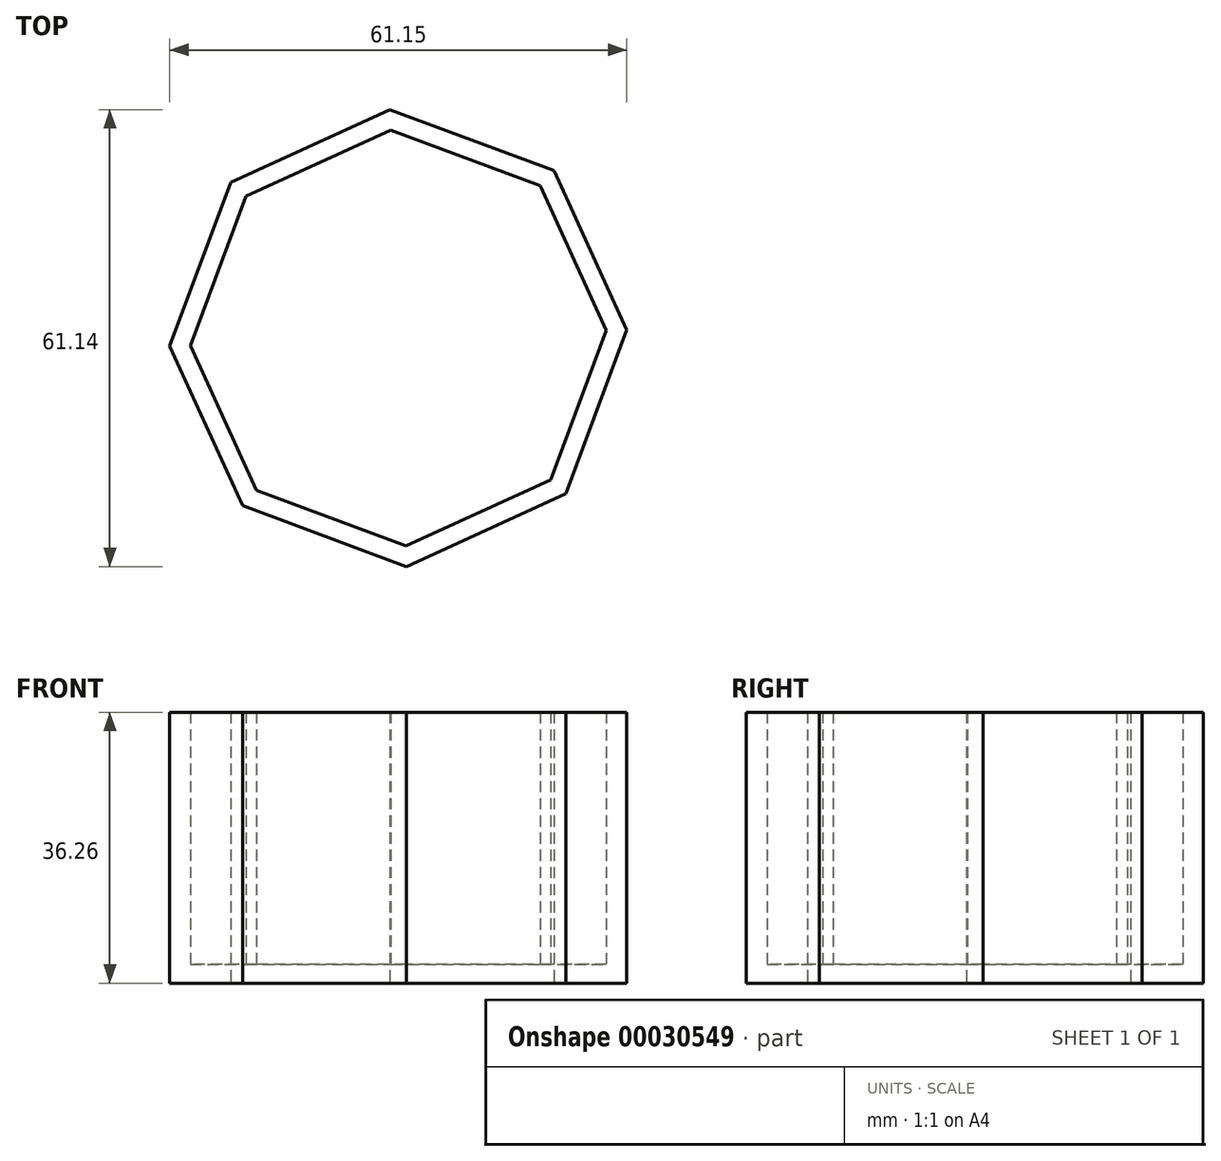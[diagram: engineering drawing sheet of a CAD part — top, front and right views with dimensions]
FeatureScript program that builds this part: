
annotation { "Feature Type Name" : "Feature", "Feature Type Description" : "" }
export const myFeature = defineFeature(function(context is Context, id is Id, definition is map)
    precondition{}
    {
        {
            var Q0;
            Q0=qCreatedBy(makeId("Top.planeOp"),FACE);
            var sketch = newSketch(context, id + "F0", { "sketchPlane" : qUnion([Q0])});
            skCircle(sketch, "E0.cCircle", {"center": v(-38.84, -19.02) * mm, "radius": 28.26 * mm, "construction": true});
            skLineSegment(sketch, "E0.0", {"start": v(-18, 3.38) * mm, "end": v(-8.26, -17.92) * mm});
            skLineSegment(sketch, "E0.1", {"start": v(-8.26, -17.92) * mm, "end": v(-16.44, -39.86) * mm});
            skLineSegment(sketch, "E0.2", {"start": v(-16.44, -39.86) * mm, "end": v(-37.74, -49.6) * mm});
            skLineSegment(sketch, "E0.3", {"start": v(-37.74, -49.6) * mm, "end": v(-59.68, -41.42) * mm});
            skLineSegment(sketch, "E0.4", {"start": v(-59.68, -41.42) * mm, "end": v(-69.41, -20.12) * mm});
            skLineSegment(sketch, "E0.5", {"start": v(-69.41, -20.12) * mm, "end": v(-61.23, 1.82) * mm});
            skLineSegment(sketch, "E0.6", {"start": v(-61.23, 1.82) * mm, "end": v(-39.94, 11.55) * mm});
            skLineSegment(sketch, "E0.7", {"start": v(-39.94, 11.55) * mm, "end": v(-18, 3.38) * mm});
            skPoint(sketch, "E0.0.midPoint", {"position": v(-13.13, -7.27) * mm});
            skSolve(sketch);
        }
        {
            var Q0;
            Q0 = qSketchRegion(id + "F0", true);
            extrude(context, id + "F1", {"entities" : qUnion([Q0]), "depth" : 10.86 * mm});
        }
        {
            var Q0;
            Q0=makeQuery(id+"F1.opExtrude","CAP_FACE",FACE,{"disambiguationData":[OSD([sQuery(id+"F0.wireOp",EDGE,"E0.0"),sQuery(id+"F0.wireOp",EDGE,"E0.1"),sQuery(id+"F0.wireOp",EDGE,"E0.2"),sQuery(id+"F0.wireOp",EDGE,"E0.3"),sQuery(id+"F0.wireOp",EDGE,"E0.4"),sQuery(id+"F0.wireOp",EDGE,"E0.5"),sQuery(id+"F0.wireOp",EDGE,"E0.6"),sQuery(id+"F0.wireOp",EDGE,"E0.7")])],"isStart":false});
            extrude(context, id + "F2", {"entities" : qUnion([Q0]), "operationType" : NewBodyOperationType.ADD, "depth" : 25.4 * mm});
        }
        {
            var Q0;
            Q0=makeQuery(id+"F2.opExtrude","CAP_FACE",FACE,{"disambiguationData":[OSD([sQuery(id+"F0.wireOp",EDGE,"E0.0"),sQuery(id+"F0.wireOp",EDGE,"E0.1"),sQuery(id+"F0.wireOp",EDGE,"E0.2"),sQuery(id+"F0.wireOp",EDGE,"E0.3"),sQuery(id+"F0.wireOp",EDGE,"E0.4"),sQuery(id+"F0.wireOp",EDGE,"E0.5"),sQuery(id+"F0.wireOp",EDGE,"E0.6"),sQuery(id+"F0.wireOp",EDGE,"E0.7")])],"isStart":false});
            shell(context, id + "F3", {"entities" : qUnion([Q0]), "thickness" : 2.54 * mm});
        }
    });
